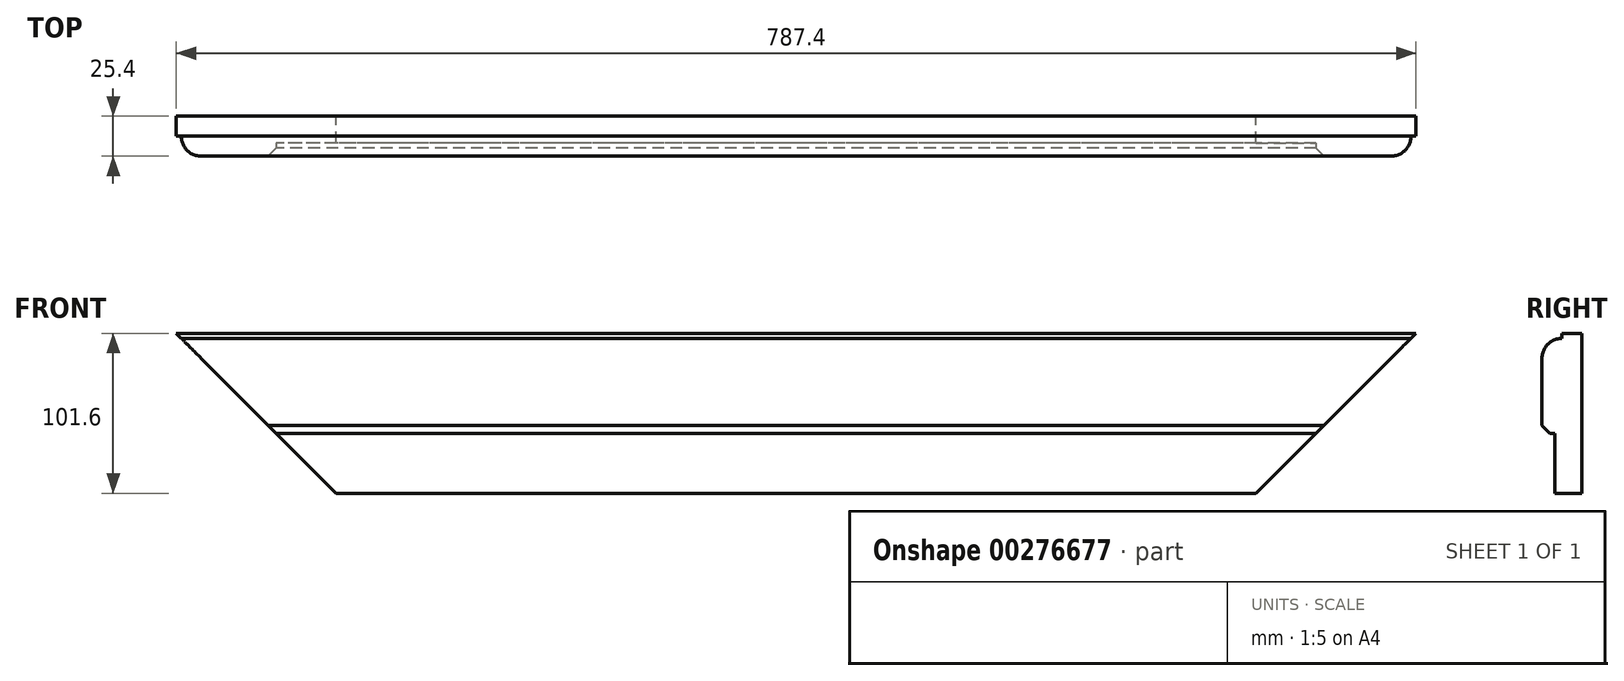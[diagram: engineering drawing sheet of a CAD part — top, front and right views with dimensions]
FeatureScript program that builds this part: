
annotation { "Feature Type Name" : "Feature", "Feature Type Description" : "" }
export const myFeature = defineFeature(function(context is Context, id is Id, definition is map)
    precondition{}
    {
        {
            var Q0;
            Q0=qCreatedBy(makeId("Right.planeOp"),FACE);
            var sketch = newSketch(context, id + "F0", { "sketchPlane" : qUnion([Q0])});
            skLineSegment(sketch, "E0.bottom", {"start": v(0, 0) * mm, "end": v(-17.14, 0) * mm});
            skLineSegment(sketch, "E0.top", {"start": v(0, 101.6) * mm, "end": v(-12.7, 101.6) * mm});
            skLineSegment(sketch, "E0.left", {"start": v(0, 0) * mm, "end": v(0, 101.6) * mm});
            skLineSegment(sketch, "E0.right", {"start": v(-25.4, 38.1) * mm, "end": v(-25.4, 85.72) * mm});
            skLineSegment(sketch, "E1", {"start": v(-17.14, 0) * mm, "end": v(-17.14, 38.1) * mm});
            skLineSegment(sketch, "E2", {"start": v(-17.14, 38.1) * mm, "end": v(-25.4, 38.1) * mm});
            skLineSegment(sketch, "E3", {"start": v(-12.7, 101.6) * mm, "end": v(-12.7, 98.42) * mm});
            skArc(sketch, "E4", {"start": v(-12.7, 98.43) * mm, "mid": v(-21.68, 94.7) * mm, "end": v(-25.4, 85.72) * mm});
            skSolve(sketch);
        }
        {
            var Q0;
            Q0=makeQuery(id+"F0.imprint","IMPRINT",FACE,{"disambiguationData":[TD([[makeQuery(id+"F0.imprint","IMPRINT",EDGE,{"derivedFrom":sQuery(id+"F0.wireOp",EDGE,"E0.bottom")}),-1.0]])]});
            extrude(context, id + "F1", {"entities" : qUnion([Q0]), "depth" : 787.4 * mm});
        }
        {
            var Q0;
            Q0=makeQuery(id+"F1.opExtrude","SWEPT_FACE",FACE,{"disambiguationData":[OSD([sQuery(id+"F0.wireOp",EDGE,"E0.left")])]});
            var sketch = newSketch(context, id + "F2", { "sketchPlane" : qUnion([Q0])});
            skLineSegment(sketch, "E5", {"start": v(-787.4, 101.6) * mm, "end": v(-685.8, 0) * mm});
            skLineSegment(sketch, "E6", {"start": v(0, 101.6) * mm, "end": v(-101.6, 0) * mm});
            skSolve(sketch);
        }
        {
            var Q0;
            Q0=qSketchRegion(id+"F2",true);
            var Q1;
            {var subQ0=sQuery(id+"F2.wireOp",EDGE,"E5");Q1=makeQuery(id+"F2.imprint","IMPRINT",FACE,{"disambiguationData":[TD([[makeQuery(id+"F2.imprint","IMPRINT",EDGE,{"derivedFrom":subQ0}),-1.0]])]});}
            var Q2;
            {var subQ0=sQuery(id+"F2.wireOp",EDGE,"E6");Q2=makeQuery(id+"F2.imprint","IMPRINT",FACE,{"disambiguationData":[TD([[makeQuery(id+"F2.imprint","IMPRINT",EDGE,{"derivedFrom":subQ0}),1.0]])]});}
            extrude(context, id + "F3", {"entities" : qUnion([Q0, Q1, Q2]), "operationType" : NewBodyOperationType.REMOVE, "oppositeDirection" : true, "depth" : 25.4 * mm});
        }
        {
            var Q0;
            Q0=makeQuery(id+"F1.opExtrude","SWEPT_EDGE",EDGE,{"disambiguationData":[OSD([sQuery(id+"F0.wireOp",EDGE,"E0.right"),sQuery(id+"F0.wireOp",EDGE,"E2")])]});
            chamfer(context, id + "F4", {"entities" : qUnion([Q0]), "width" : 5.08 * mm, "tangentPropagation" : true});
        }
    });
